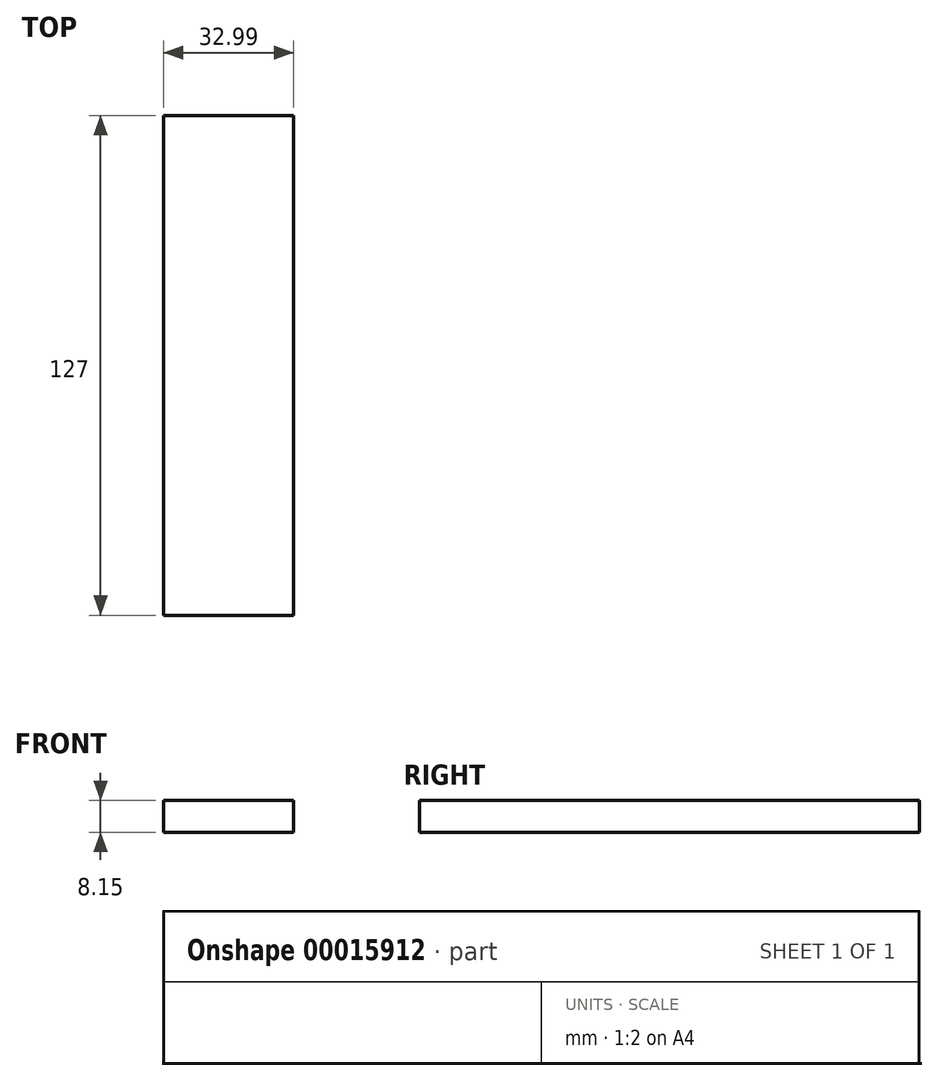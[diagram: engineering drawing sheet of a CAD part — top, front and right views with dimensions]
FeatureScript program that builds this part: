
annotation { "Feature Type Name" : "Feature", "Feature Type Description" : "" }
export const myFeature = defineFeature(function(context is Context, id is Id, definition is map)
    precondition{}
    {
        {
            var Q0;
            Q0=qCreatedBy(makeId("Front.planeOp"),FACE);
            var sketch = newSketch(context, id + "F0", { "sketchPlane" : qUnion([Q0])});
            skLineSegment(sketch, "E0.bottom", {"start": v(-23.62, 12.22) * mm, "end": v(9.37, 12.22) * mm});
            skLineSegment(sketch, "E0.top", {"start": v(-23.62, 4.07) * mm, "end": v(9.37, 4.07) * mm});
            skLineSegment(sketch, "E0.left", {"start": v(-23.62, 12.22) * mm, "end": v(-23.62, 4.07) * mm});
            skLineSegment(sketch, "E0.right", {"start": v(9.37, 12.22) * mm, "end": v(9.37, 4.07) * mm});
            skSolve(sketch);
        }
        {
            var Q0;
            Q0=makeQuery(id+"F0.imprint","IMPRINT",FACE,{"disambiguationData":[TD([[makeQuery(id+"F0.imprint","IMPRINT",EDGE,{"derivedFrom":sQuery(id+"F0.wireOp",EDGE,"E0.bottom")}),-1.0]])]});
            extrude(context, id + "F1", {"entities" : qUnion([Q0]), "depth" : 127 * mm});
        }
    });
